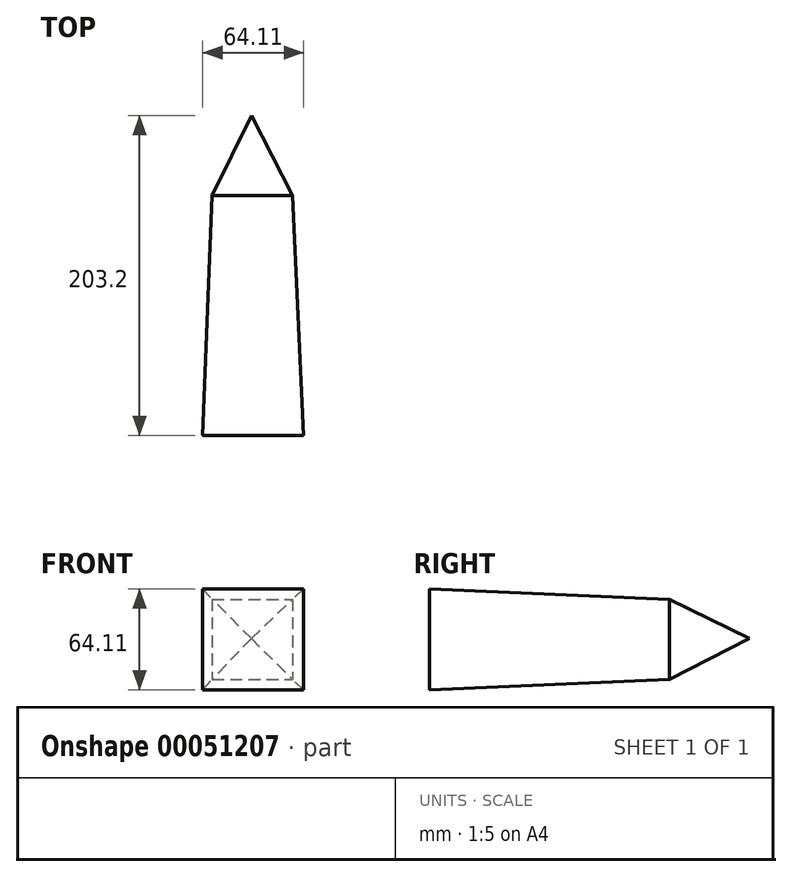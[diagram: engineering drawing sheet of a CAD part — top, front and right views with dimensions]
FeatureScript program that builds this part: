
annotation { "Feature Type Name" : "Feature", "Feature Type Description" : "" }
export const myFeature = defineFeature(function(context is Context, id is Id, definition is map)
    precondition{}
    {
        {
            var Q0;
            Q0=qCreatedBy(makeId("Front.planeOp"),FACE);
            var sketch = newSketch(context, id + "F0", { "sketchPlane" : qUnion([Q0])});
            skLineSegment(sketch, "E0.bottom", {"start": v(-35.57, 34.22) * mm, "end": v(15.23, 34.22) * mm});
            skLineSegment(sketch, "E0.top", {"start": v(-35.57, -16.58) * mm, "end": v(15.23, -16.58) * mm});
            skLineSegment(sketch, "E0.left", {"start": v(-35.57, 34.22) * mm, "end": v(-35.57, -16.58) * mm});
            skLineSegment(sketch, "E0.right", {"start": v(15.23, 34.22) * mm, "end": v(15.23, -16.58) * mm});
            skSolve(sketch);
        }
        {
            var Q0;
            Q0=makeQuery(id+"F0.imprint","IMPRINT",FACE,{"disambiguationData":[TD([[makeQuery(id+"F0.imprint","IMPRINT",EDGE,{"derivedFrom":sQuery(id+"F0.wireOp",EDGE,"E0.bottom")}),-1.0]])]});
            cPlane(context, id + "F1", {"entities" : qUnion([Q0]), "cplaneType" : CPlaneType.OFFSET, "offset" : 152.4 * mm, "width" : 152.4 * mm, "height" : 152.4 * mm});
        }
        {
            var Q0;
            Q0=qCreatedBy(id+"F1.planeOp",FACE);
            var sketch = newSketch(context, id + "F2", { "sketchPlane" : qUnion([Q0])});
            skLineSegment(sketch, "E1.bottom", {"start": v(-41.67, 40.73) * mm, "end": v(22.44, 40.73) * mm});
            skLineSegment(sketch, "E1.top", {"start": v(-41.67, -23.38) * mm, "end": v(22.44, -23.38) * mm});
            skLineSegment(sketch, "E1.left", {"start": v(-41.67, 40.73) * mm, "end": v(-41.67, -23.38) * mm});
            skLineSegment(sketch, "E1.right", {"start": v(22.44, 40.73) * mm, "end": v(22.44, -23.38) * mm});
            skSolve(sketch);
        }
        {
            var Q0;
            Q0=makeQuery(id+"F2.imprint","IMPRINT",FACE,{"disambiguationData":[TD([[makeQuery(id+"F2.imprint","IMPRINT",EDGE,{"derivedFrom":sQuery(id+"F2.wireOp",EDGE,"E1.bottom")}),-1.0]])]});
            var Q1;
            Q1=makeQuery(id+"F0.imprint","IMPRINT",FACE,{"disambiguationData":[TD([[makeQuery(id+"F0.imprint","IMPRINT",EDGE,{"derivedFrom":sQuery(id+"F0.wireOp",EDGE,"E0.bottom")}),-1.0]])]});
            loft(context, id + "F3", {"sheetProfilesArray" : [{ "sheetProfileEntities" : qUnion([Q0]) }, { "sheetProfileEntities" : qUnion([Q1]) }]});
        }
        {
            var Q0;
            Q0=makeQuery(id+"F3.opLoft","CAP_FACE",FACE,{"disambiguationData":[OSD([makeQuery(id+"F0.imprint","IMPRINT",FACE,{"disambiguationData":[TD([[makeQuery(id+"F0.imprint","IMPRINT",EDGE,{"derivedFrom":sQuery(id+"F0.wireOp",EDGE,"E0.bottom")}),-1.0]])]})])],"isStart":true});
            cPlane(context, id + "F4", {"entities" : qUnion([Q0]), "cplaneType" : CPlaneType.OFFSET, "offset" : 50.8 * mm, "width" : 152.4 * mm, "height" : 152.4 * mm});
        }
        {
            var Q0;
            Q0=qCreatedBy(id+"F4.planeOp",FACE);
            var sketch = newSketch(context, id + "F5", { "sketchPlane" : qUnion([Q0])});
            skPoint(sketch, "E2", {"position": v(10.73, 9.24) * mm});
            skSolve(sketch);
        }
        {
            var Q1;
            Q1=sQuery(id+"F5.wireOp",VERTEX,"E2");
            var Q2;
            Q2=makeQuery(id+"F3.opLoft","CAP_FACE",FACE,{"disambiguationData":[OSD([makeQuery(id+"F0.imprint","IMPRINT",FACE,{"disambiguationData":[TD([[makeQuery(id+"F0.imprint","IMPRINT",EDGE,{"derivedFrom":sQuery(id+"F0.wireOp",EDGE,"E0.bottom")}),-1.0]])]})])],"isStart":true});
            loft(context, id + "F6", {"operationType" : NewBodyOperationType.ADD, "sheetProfilesArray" : [{ "sheetProfileEntities" : qUnion([Q1]) }, { "sheetProfileEntities" : qUnion([Q2]) }]});
        }
    });
